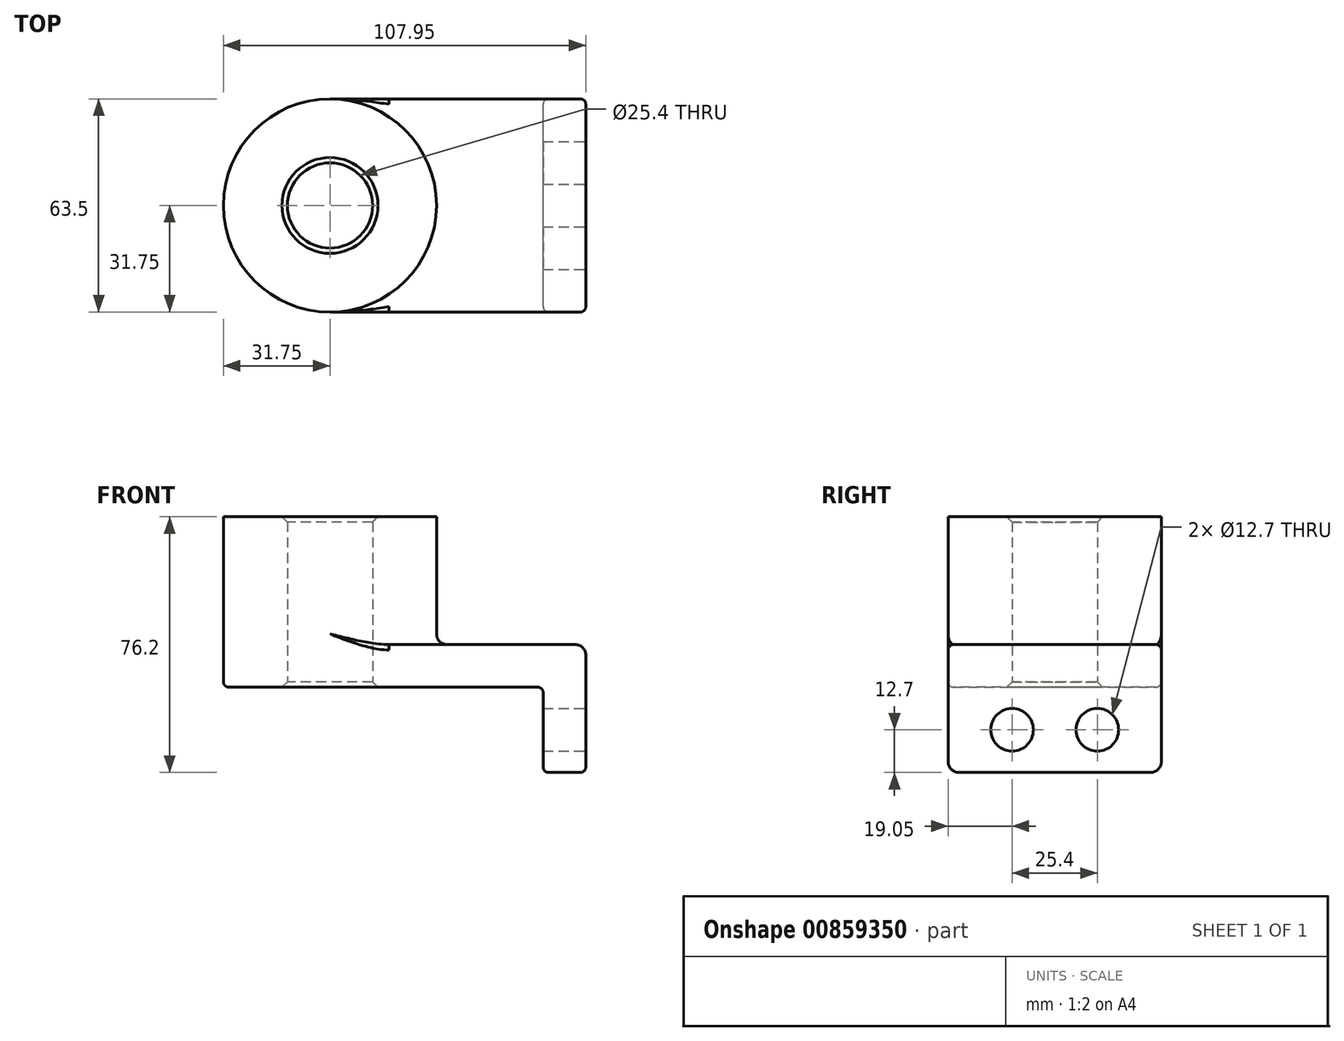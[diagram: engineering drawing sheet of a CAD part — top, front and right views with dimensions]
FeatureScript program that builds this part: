
annotation { "Feature Type Name" : "Feature", "Feature Type Description" : "" }
export const myFeature = defineFeature(function(context is Context, id is Id, definition is map)
    precondition{}
    {
        {
            var Q0;
            Q0=qCreatedBy(makeId("Top.planeOp"),FACE);
            var sketch = newSketch(context, id + "F0", { "sketchPlane" : qUnion([Q0])});
            skLineSegment(sketch, "E0.bottom", {"start": v(38.1, 31.75) * mm, "end": v(-38.1, 31.75) * mm});
            skLineSegment(sketch, "E0.top", {"start": v(38.1, -31.75) * mm, "end": v(-38.1, -31.75) * mm});
            skLineSegment(sketch, "E0.left", {"start": v(38.1, 31.75) * mm, "end": v(38.1, -31.75) * mm});
            skLineSegment(sketch, "E0.right", {"start": v(-38.1, 31.75) * mm, "end": v(-38.1, -31.75) * mm});
            skPoint(sketch, "E0.middle", {"position": v(0, 0) * mm});
            skCircle(sketch, "E1", {"center": v(-38.1, 0) * mm, "radius": 31.75 * mm});
            skCircle(sketch, "E2", {"center": v(-38.1, 0) * mm, "radius": 12.7 * mm});
            skSolve(sketch);
        }
        {
            var Q0;
            Q0 = qSketchRegion(id + "F0", true);
            extrude(context, id + "F1", {"entities" : qUnion([Q0]), "depth" : 12.7 * mm, "offsetDistance" : 25.4 * mm});
        }
        {
            var Q0;
            {var subQ1=sQuery(id+"F0.wireOp",EDGE,"E0.right");var subQ3=sQuery(id+"F0.wireOp",EDGE,"E2");var subQ4=makeQuery(id+"F0.imprint","INTERSECT",VERTEX,{"disambiguationData":[OD(0.0)],"derivedFrom":[subQ1,subQ3]});Q0=makeQuery(id+"F0.imprint","IMPRINT",FACE,{"disambiguationData":[TD([[makeQuery(id+"F0.imprint","IMPRINT",EDGE,{"disambiguationData":[TD([[subQ4,-1.0]])],"derivedFrom":subQ3}),-1.0]])]});}
            var Q1;
            {var subQ1=sQuery(id+"F0.wireOp",EDGE,"E0.right");var subQ3=sQuery(id+"F0.wireOp",EDGE,"E2");var subQ4=makeQuery(id+"F0.imprint","INTERSECT",VERTEX,{"disambiguationData":[OD(0.0)],"derivedFrom":[subQ1,subQ3]});Q1=makeQuery(id+"F0.imprint","IMPRINT",FACE,{"disambiguationData":[TD([[makeQuery(id+"F0.imprint","IMPRINT",EDGE,{"disambiguationData":[TD([[subQ4,1.0]])],"derivedFrom":subQ3}),-1.0]])]});}
            extrude(context, id + "F2", {"entities" : qUnion([Q0, Q1]), "operationType" : NewBodyOperationType.ADD, "depth" : 50.8 * mm, "offsetDistance" : 25.4 * mm});
        }
        {
            var Q0;
            Q0=makeQuery(id+"F1.opExtrude","SWEPT_FACE",FACE,{"disambiguationData":[OSD([sQuery(id+"F0.wireOp",EDGE,"E0.left")])]});
            var sketch = newSketch(context, id + "F3", { "sketchPlane" : qUnion([Q0])});
            skLineSegment(sketch, "E3.bottom", {"start": v(-31.75, 12.7) * mm, "end": v(31.75, 12.7) * mm});
            skLineSegment(sketch, "E3.top", {"start": v(-31.75, -25.4) * mm, "end": v(31.75, -25.4) * mm});
            skLineSegment(sketch, "E3.left", {"start": v(-31.75, 12.7) * mm, "end": v(-31.75, -25.4) * mm});
            skLineSegment(sketch, "E3.right", {"start": v(31.75, 12.7) * mm, "end": v(31.75, -25.4) * mm});
            skCircle(sketch, "E4", {"center": v(-12.7, -12.7) * mm, "radius": 6.35 * mm});
            skLineSegment(sketch, "E5", {"start": v(0, 0) * mm, "end": v(0, -33.55) * mm, "construction": true});
            skPoint(sketch, "E5.endSnap0", {"position": v(0, -25.4) * mm});
            skCircle(sketch, "E6.MirrorC", {"center": v(12.7, -12.7) * mm, "radius": 6.35 * mm});
            skSolve(sketch);
        }
        {
            var Q0;
            Q0 = qSketchRegion(id + "F3", true);
            extrude(context, id + "F4", {"entities" : qUnion([Q0]), "operationType" : NewBodyOperationType.ADD, "oppositeDirection" : true, "depth" : 12.7 * mm, "offsetDistance" : 25.4 * mm});
        }
        {
            var Q0;
            {var subQ0=sQuery(id+"F0.wireOp",EDGE,"E1");Q0=makeQuery(id+"F2.boolean.opBoolean","INTERSECT",EDGE,{"derivedFrom":[makeQuery(id+"F1.opExtrude","CAP_FACE",FACE,{"disambiguationData":[OSD([sQuery(id+"F0.wireOp",EDGE,"E0.bottom"),sQuery(id+"F0.wireOp",EDGE,"E0.top"),sQuery(id+"F0.wireOp",EDGE,"E0.left"),subQ0,sQuery(id+"F0.wireOp",EDGE,"E2")])],"isStart":false}),makeQuery(id+"F2.opExtrude","SWEPT_FACE",FACE,{"disambiguationData":[OSD([subQ0])]})]});}
            var Q1;
            Q1=makeQuery(id+"F1.opExtrude","CAP_EDGE",EDGE,{"disambiguationData":[OSD([sQuery(id+"F0.wireOp",EDGE,"E0.left")])],"isStart":false});
            var Q2;
            Q2=makeQuery(id+"F4.opExtrude","SWEPT_EDGE",EDGE,{"disambiguationData":[OSD([sQuery(id+"F3.wireOp",EDGE,"E3.top"),sQuery(id+"F3.wireOp",EDGE,"E3.left")])]});
            var Q3;
            Q3=makeQuery(id+"F4.opExtrude","SWEPT_EDGE",EDGE,{"disambiguationData":[OSD([sQuery(id+"F3.wireOp",EDGE,"E3.top"),sQuery(id+"F3.wireOp",EDGE,"E3.right")])]});
            fillet(context, id + "F5", {"entities" : qUnion([Q0, Q1, Q2, Q3]), "radius" : 3.17 * mm, "tangentPropagation" : true, "allowEdgeOverflow" : false});
        }
        {
            var Q0;
            Q0=makeQuery(id+"F4.boolean.opBoolean","INTERSECT",EDGE,{"derivedFrom":[makeQuery(id+"F1.opExtrude","CAP_FACE",FACE,{"disambiguationData":[OSD([sQuery(id+"F0.wireOp",EDGE,"E0.bottom"),sQuery(id+"F0.wireOp",EDGE,"E0.top"),sQuery(id+"F0.wireOp",EDGE,"E0.left"),sQuery(id+"F0.wireOp",EDGE,"E1"),sQuery(id+"F0.wireOp",EDGE,"E2")])],"isStart":true}),makeQuery(id+"F4.opExtrude","CAP_FACE",FACE,{"disambiguationData":[OSD([sQuery(id+"F3.wireOp",EDGE,"E3.bottom"),sQuery(id+"F3.wireOp",EDGE,"E3.top"),sQuery(id+"F3.wireOp",EDGE,"E3.left"),sQuery(id+"F3.wireOp",EDGE,"E3.right"),sQuery(id+"F3.wireOp",EDGE,"E4"),sQuery(id+"F3.wireOp",EDGE,"E6.MirrorC")])],"isStart":false})]});
            var Q1;
            Q1=makeQuery(id+"F4.boolean.opBoolean","MERGE",FACE,{"derivedFrom":[makeQuery(id+"F1.opExtrude","SWEPT_FACE",FACE,{"disambiguationData":[OSD([sQuery(id+"F0.wireOp",EDGE,"E0.top")])]}),makeQuery(id+"F4.opExtrude","SWEPT_FACE",FACE,{"disambiguationData":[OSD([sQuery(id+"F3.wireOp",EDGE,"E3.left")])]})]});
            fillet(context, id + "F6", {"entities" : qUnion([Q0, Q1]), "radius" : 1.59 * mm, "tangentPropagation" : true, "allowEdgeOverflow" : false});
        }
        {
            var Q0;
            {var subQ0=sQuery(id+"F0.wireOp",EDGE,"E2");Q0=makeQuery(id+"F2.boolean.opBoolean","MERGE",FACE,{"derivedFrom":[makeQuery(id+"F1.opExtrude","SWEPT_FACE",FACE,{"disambiguationData":[OSD([subQ0])]}),makeQuery(id+"F2.opExtrude","SWEPT_FACE",FACE,{"disambiguationData":[OSD([subQ0])]})]});}
            chamfer(context, id + "F7", {"entities" : qUnion([Q0]), "width" : 1.59 * mm, "tangentPropagation" : true});
        }
    });
